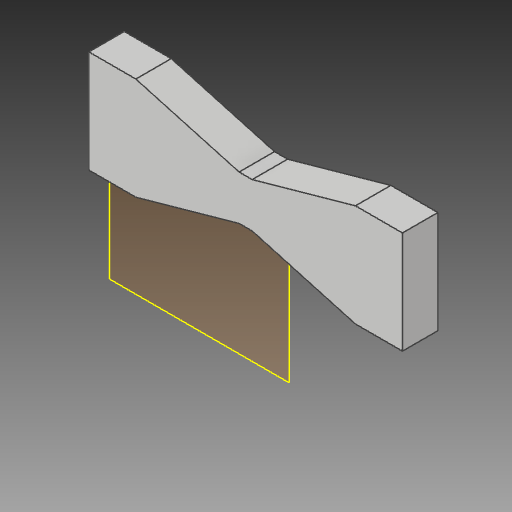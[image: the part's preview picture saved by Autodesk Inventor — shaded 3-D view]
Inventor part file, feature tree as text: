
AUTODESK INVENTOR PART (.ipt)
format: ipt  version: 2017 (Build 210142000, 142)  size: 111,616 bytes
history: native  units: mm
features: other x4, plane x2, sketch x1, extrude x1, mirror x1, reference x1
ambient origin geometry x8: Origin, YZ Plane, XZ Plane, XY Plane, X Axis, Y Axis, Z Axis, Center Point
bodies: Solid1 (feature_tree)
feature tree (10):
  plane  "Work Plane1"
  sketch  "Sketch1"  dims[d0=0.6mm d1=3.25mm d2=0.0mm]
  plane  "Work Plane2"
  extrude  "Extrusion1"  Depth=3.25mm TaperAngle=0.0deg
  mirror  "Mirror2"
  reference  "Reference1"
  other  "<userpath>\Dropbox\Arduino\arduinoLED_BGLighting\Hardware\Light Holder.iam"
  other  "Light Holder.iam"
  other  "Top Clip:1"
  other  "<userpath>\Desktop\Arduino\ambientLighting_stateMachine\Hardware\Light Holder.iam"
